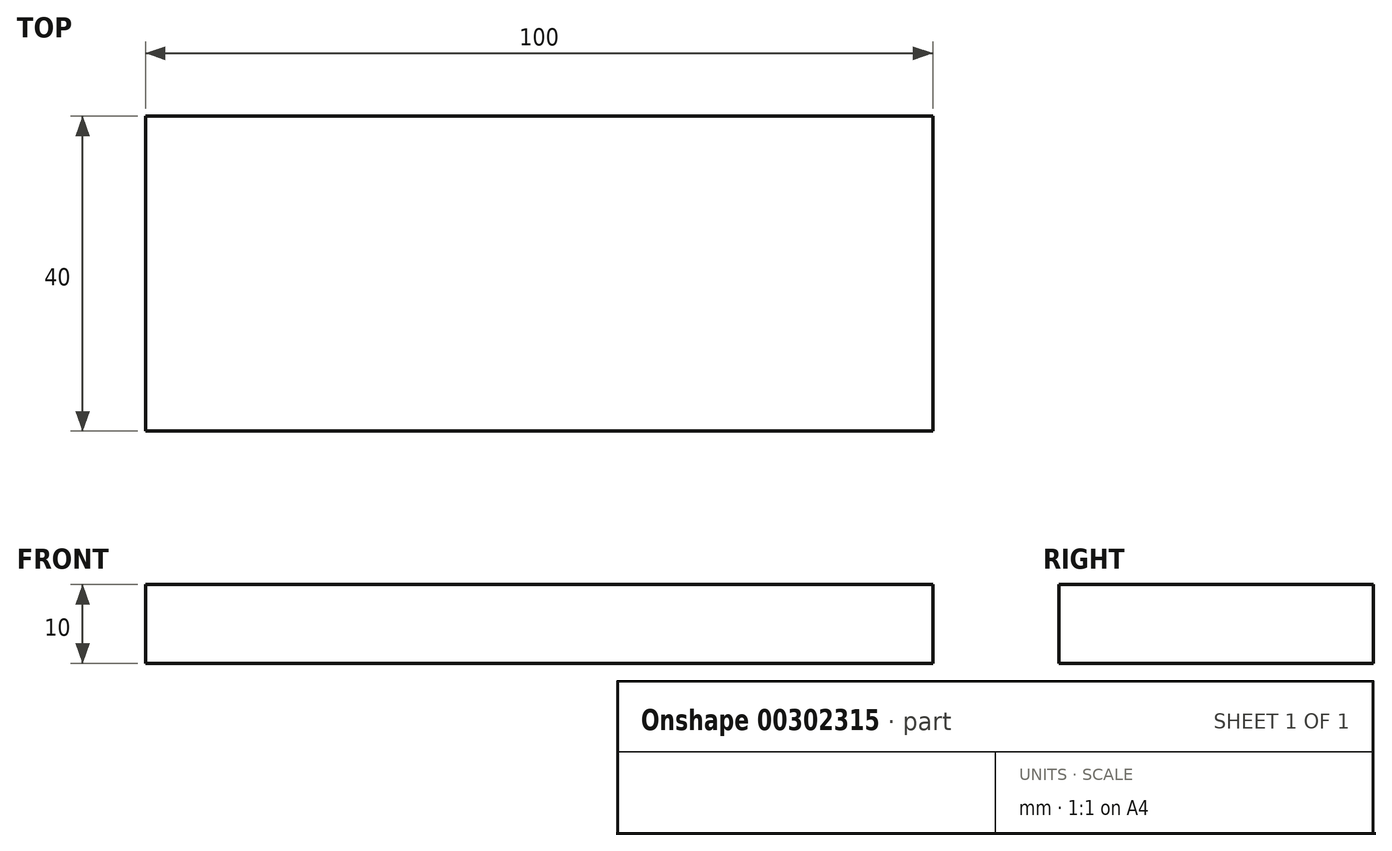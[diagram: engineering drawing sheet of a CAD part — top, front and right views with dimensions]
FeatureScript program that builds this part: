
annotation { "Feature Type Name" : "Feature", "Feature Type Description" : "" }
export const myFeature = defineFeature(function(context is Context, id is Id, definition is map)
    precondition{}
    {
        {
            var Q0;
            Q0=qCreatedBy(makeId("Top.planeOp"),FACE);
            var sketch = newSketch(context, id + "F0", { "sketchPlane" : qUnion([Q0])});
            skLineSegment(sketch, "E0.bottom", {"start": v(-100, 40) * mm, "end": v(0, 40) * mm});
            skLineSegment(sketch, "E0.top", {"start": v(-100, 0) * mm, "end": v(0, 0) * mm});
            skLineSegment(sketch, "E0.left", {"start": v(-100, 40) * mm, "end": v(-100, 0) * mm});
            skLineSegment(sketch, "E0.right", {"start": v(0, 40) * mm, "end": v(0, 0) * mm});
            skSolve(sketch);
        }
        {
            var Q0;
            Q0=qSketchRegion(id+"F0",true);
            extrude(context, id + "F1", {"entities" : qUnion([Q0]), "depth" : 10 * mm});
        }
        {
            var Q0;
            Q0=makeQuery(id+"F1.opExtrude","SWEPT_FACE",FACE,{"disambiguationData":[OSD([sQuery(id+"F0.wireOp",EDGE,"E0.top")])]});
            var sketch = newSketch(context, id + "F2", { "sketchPlane" : qUnion([Q0])});
            skLineSegment(sketch, "E1", {"start": v(-70, 0) * mm, "end": v(-70, 35) * mm});
            skArc(sketch, "E2", {"start": v(-70, 35) * mm, "mid": v(-50, 55) * mm, "end": v(-30, 35) * mm});
            skLineSegment(sketch, "E3", {"start": v(-30, 35) * mm, "end": v(-30, 0) * mm});
            skLineSegment(sketch, "E4", {"start": v(-70, 0) * mm, "end": v(-30, 0) * mm});
            skSolve(sketch);
        }
    });
